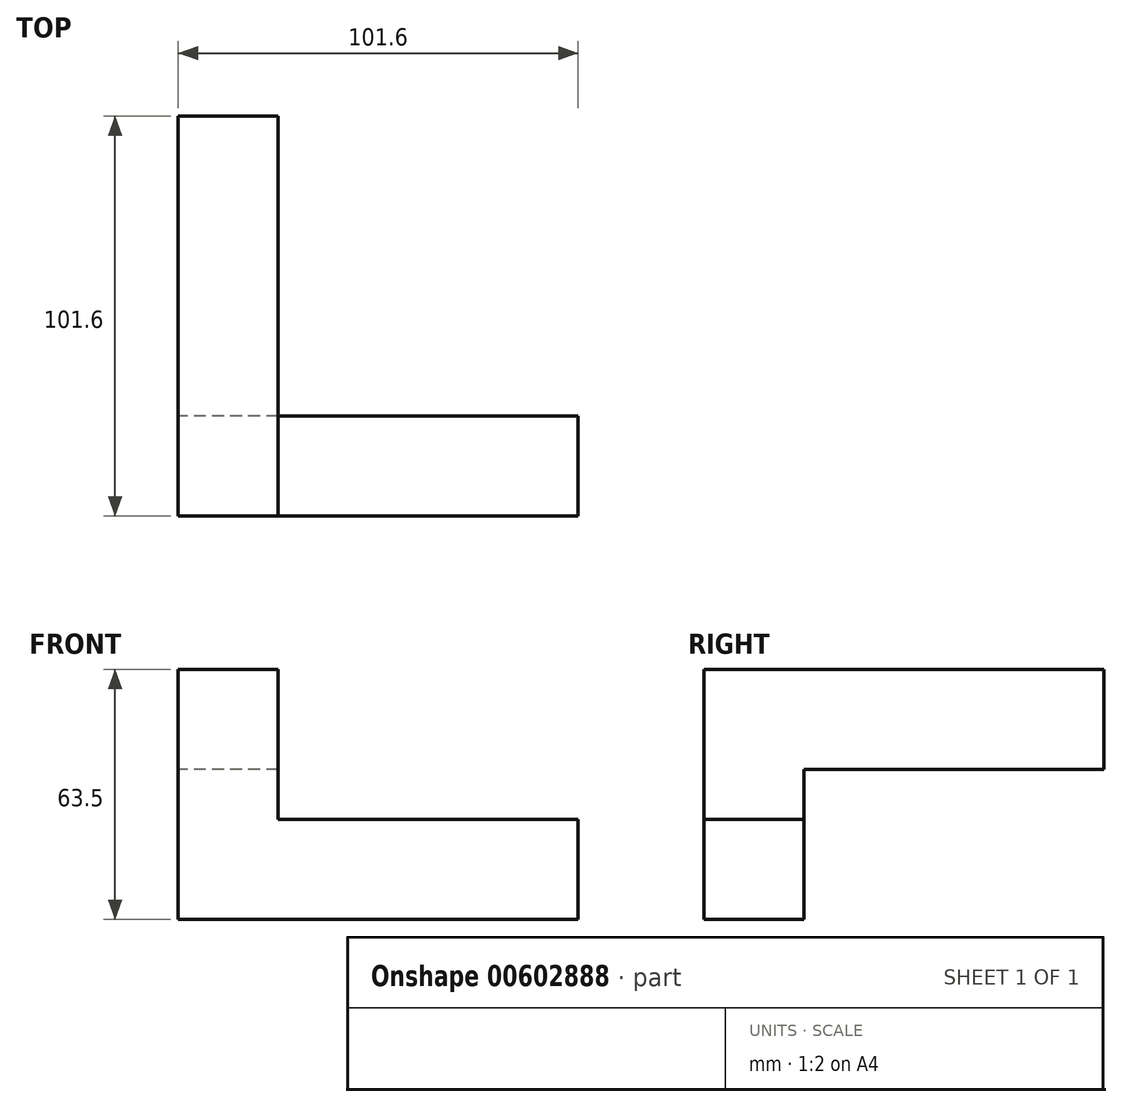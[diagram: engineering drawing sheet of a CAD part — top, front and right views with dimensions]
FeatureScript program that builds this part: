
annotation { "Feature Type Name" : "Feature", "Feature Type Description" : "" }
export const myFeature = defineFeature(function(context is Context, id is Id, definition is map)
    precondition{}
    {
        {
            var Q0;
            Q0=qCreatedBy(makeId("Front.planeOp"),FACE);
            var sketch = newSketch(context, id + "F0", { "sketchPlane" : qUnion([Q0])});
            skLineSegment(sketch, "E0.bottom", {"start": v(0, 0) * mm, "end": v(25.4, 0) * mm});
            skLineSegment(sketch, "E0.top", {"start": v(0, 63.5) * mm, "end": v(25.4, 63.5) * mm});
            skLineSegment(sketch, "E0.left", {"start": v(0, 0) * mm, "end": v(0, 63.5) * mm});
            skLineSegment(sketch, "E0.right", {"start": v(25.4, 25.4) * mm, "end": v(25.4, 63.5) * mm});
            skLineSegment(sketch, "E1.bottom", {"start": v(0, 0) * mm, "end": v(101.6, 0) * mm});
            skLineSegment(sketch, "E1.top", {"start": v(25.4, 25.4) * mm, "end": v(101.6, 25.4) * mm});
            skLineSegment(sketch, "E1.left", {"start": v(0, 0) * mm, "end": v(0, 25.4) * mm});
            skLineSegment(sketch, "E1.right", {"start": v(101.6, 0) * mm, "end": v(101.6, 25.4) * mm});
            skSolve(sketch);
        }
        {
            var Q0;
            Q0=makeQuery(id+"F0.imprint","IMPRINT",FACE,{"disambiguationData":[TD([[makeQuery(id+"F0.imprint","IMPRINT",EDGE,{"derivedFrom":sQuery(id+"F0.wireOp",EDGE,"E0.top")}),-1.0]])]});
            extrude(context, id + "F1", {"entities" : qUnion([Q0]), "oppositeDirection" : true, "depth" : 25.4 * mm, "offsetDistance" : 25.4 * mm});
        }
        {
            var Q0;
            Q0=makeQuery(id+"F1.opExtrude","CAP_FACE",FACE,{"disambiguationData":[OSD([sQuery(id+"F0.wireOp",EDGE,"E0.top"),sQuery(id+"F0.wireOp",EDGE,"E0.left"),sQuery(id+"F0.wireOp",EDGE,"E0.right"),sQuery(id+"F0.wireOp",EDGE,"E1.bottom"),sQuery(id+"F0.wireOp",EDGE,"E1.top"),sQuery(id+"F0.wireOp",EDGE,"E1.left"),sQuery(id+"F0.wireOp",EDGE,"E1.right")])],"isStart":false});
            var sketch = newSketch(context, id + "F2", { "sketchPlane" : qUnion([Q0])});
            skLineSegment(sketch, "E2.bottom", {"start": v(-25.4, 63.5) * mm, "end": v(0, 63.5) * mm});
            skLineSegment(sketch, "E2.top", {"start": v(-25.4, 38.1) * mm, "end": v(0, 38.1) * mm});
            skLineSegment(sketch, "E2.left", {"start": v(-25.4, 63.5) * mm, "end": v(-25.4, 38.1) * mm});
            skLineSegment(sketch, "E2.right", {"start": v(0, 63.5) * mm, "end": v(0, 38.1) * mm});
            skSolve(sketch);
        }
        {
            var Q0;
            Q0=makeQuery(id+"F2.imprint","IMPRINT",FACE,{"disambiguationData":[TD([[makeQuery(id+"F2.imprint","IMPRINT",EDGE,{"derivedFrom":sQuery(id+"F2.wireOp",EDGE,"E2.bottom")}),1.0]])]});
            extrude(context, id + "F3", {"entities" : qUnion([Q0]), "operationType" : NewBodyOperationType.ADD, "depth" : 76.2 * mm, "offsetDistance" : 25.4 * mm});
        }
    });
